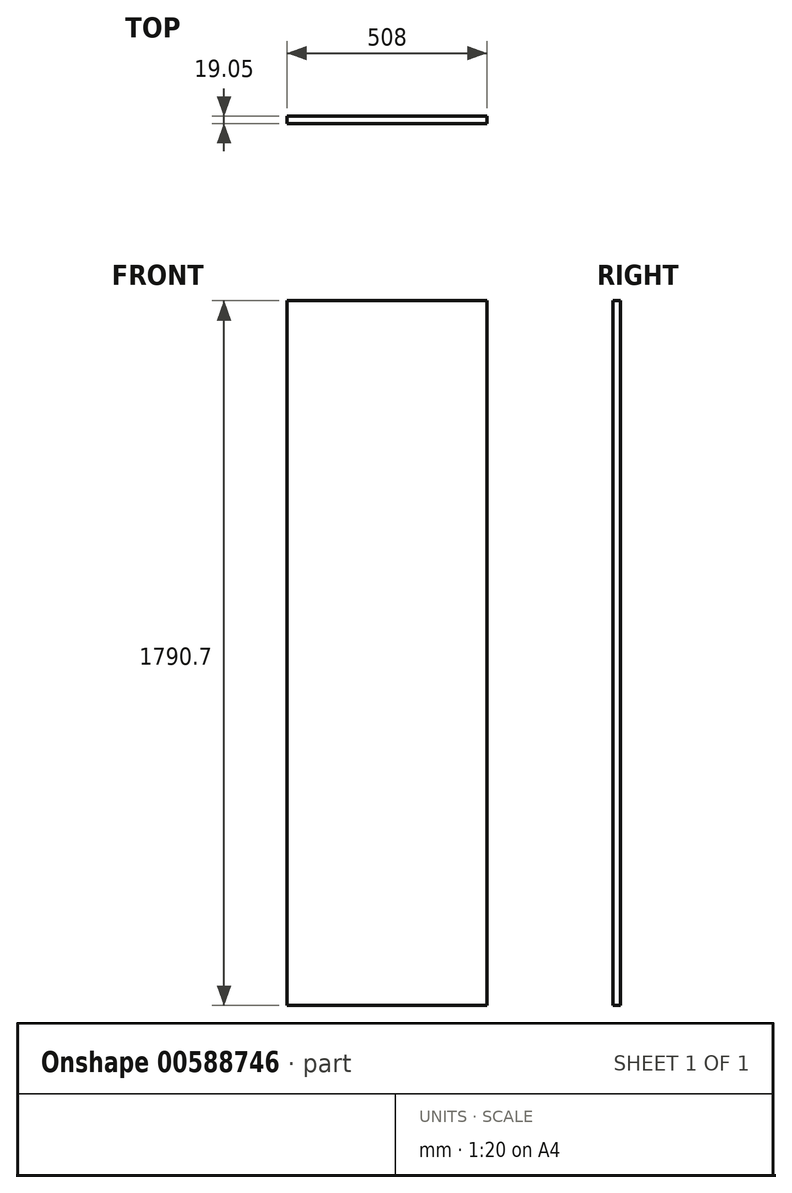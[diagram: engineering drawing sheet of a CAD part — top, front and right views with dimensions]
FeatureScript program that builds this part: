
annotation { "Feature Type Name" : "Feature", "Feature Type Description" : "" }
export const myFeature = defineFeature(function(context is Context, id is Id, definition is map)
    precondition{}
    {
        {
            var Q0;
            Q0=qCreatedBy(makeId("Front.planeOp"),FACE);
            var sketch = newSketch(context, id + "F0", { "sketchPlane" : qUnion([Q0])});
            skLineSegment(sketch, "E0.bottom", {"start": v(0, 0) * mm, "end": v(508, 0) * mm});
            skLineSegment(sketch, "E0.top", {"start": v(0, -1790.7) * mm, "end": v(508, -1790.7) * mm});
            skLineSegment(sketch, "E0.left", {"start": v(0, 0) * mm, "end": v(0, -1790.7) * mm});
            skLineSegment(sketch, "E0.right", {"start": v(508, 0) * mm, "end": v(508, -1790.7) * mm});
            skSolve(sketch);
        }
        {
            var Q0;
            Q0=makeQuery(id+"F0.imprint","IMPRINT",FACE,{"disambiguationData":[TD([[makeQuery(id+"F0.imprint","IMPRINT",EDGE,{"derivedFrom":sQuery(id+"F0.wireOp",EDGE,"E0.bottom")}),-1.0]])]});
            extrude(context, id + "F1", {"entities" : qUnion([Q0]), "oppositeDirection" : true, "depth" : 19.05 * mm, "offsetDistance" : 25.4 * mm});
        }
    });
